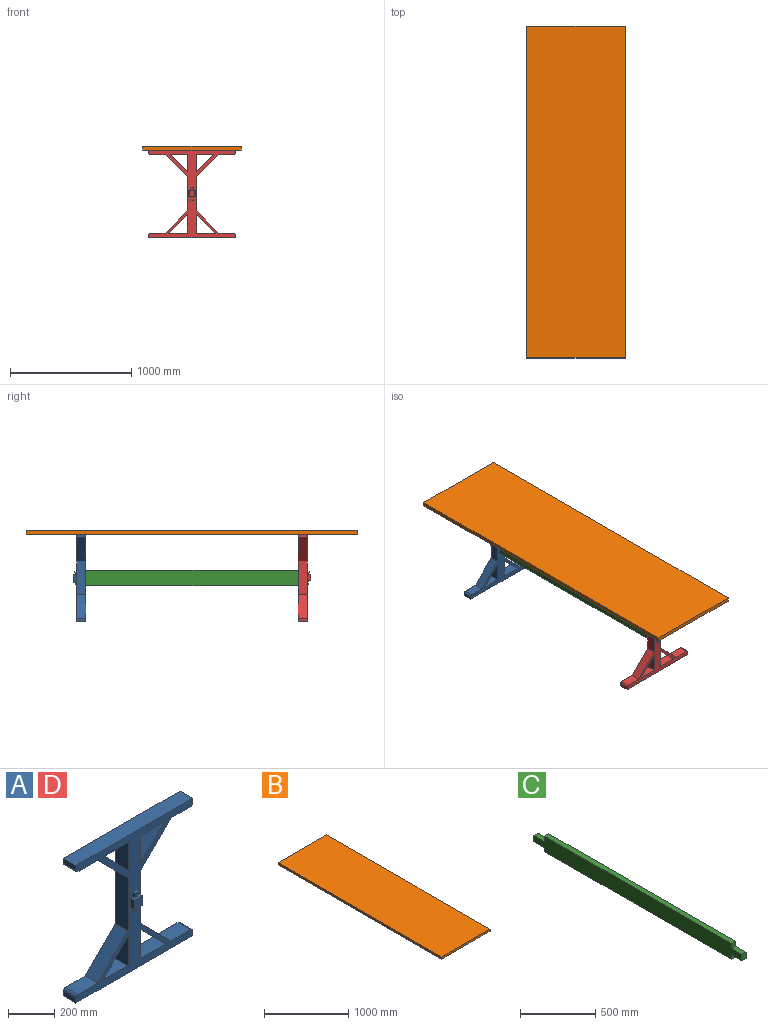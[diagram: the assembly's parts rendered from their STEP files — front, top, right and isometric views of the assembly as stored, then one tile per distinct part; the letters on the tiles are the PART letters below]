
ASSEMBLY  parts=4 mates=3
PART A: 47 faces, bbox 711.2x101.6x724.6 mm
  f0: plane 724.61x711.2mm, normal (0,-1,0), area 123856.3mm2, adj f1,f2,f3,f4,f5,f6,f7,f8
  f1: plane 50.8x25.4mm, normal (0,0,-1), area 1127mm2, adj f0,f35,f37,f38,f39,f40,f42
  f2: plane 153.23x76.2mm, normal (-1,0,0), area 11675.9mm2, adj f0,f3,f29,f34
  f3: plane 153.23x76.2mm, normal (0,0,1), area 11675.9mm2, adj f0,f2,f29,f34
  f4: plane 153.23x76.2mm, normal (0,0,1), area 11675.9mm2, adj f0,f5,f30,f34
  f5: plane 153.23x76.2mm, normal (1,0,0), area 11675.9mm2, adj f0,f4,f30,f34
  f6: plane 142.84x76.2mm, normal (1,0,0), area 10884.4mm2, adj f0,f7,f31,f34
  f7: plane 142.84x76.2mm, normal (0,0,-1), area 10884.4mm2, adj f0,f6,f31,f34
  f8: plane 142.84x142.84mm, normal (0.71,0,0.71), area 15392.8mm2, adj f0,f9,f32,f34
  f9: plane 142.84x76.2mm, normal (0,0,-1), area 10884.4mm2, adj f0,f8,f32,f34
  f10: plane 120.65x76.2mm, normal (0,0,-1), area 9193.5mm2, adj f0,f11,f33,f34
  f11: plane 184.15x184.15mm, normal (-0.71,0,-0.71), area 19844.6mm2, adj f0,f10,f12,f34
  f12: plane 280.11x76.2mm, normal (-1,0,0), area 21344.2mm2, adj f0,f11,f13,f34
  f13: plane 184.15x184.15mm, normal (-0.71,0,0.71), area 19844.6mm2, adj f0,f12,f14,f34
  f14: plane 120.65x76.2mm, normal (0,0,1), area 9193.5mm2, adj f0,f13,f15,f34
  f15: cylinder r=12.7mm len=76.2mm, axis (0,1,0), area 1520.1mm2, adj f0,f14,f16,f34
  f16: plane 76.2x25.4mm, normal (-1,0,0), area 1935.5mm2, adj f0,f15,f17,f34
  f17: plane 711.2x76.2mm, normal (0,0,-1), area 54193.4mm2, adj f0,f16,f18,f34
  f18: plane 76.2x25.4mm, normal (1,0,0), area 1935.5mm2, adj f0,f17,f19,f34
  f19: cylinder r=12.7mm len=76.2mm, axis (0,1,0), area 1520.1mm2, adj f0,f18,f20,f34
  f20: plane 120.65x76.2mm, normal (0,0,1), area 9193.5mm2, adj f0,f19,f21,f34
  f21: plane 184.15x184.15mm, normal (0.71,0,0.71), area 19844.6mm2, adj f0,f20,f22,f34
  f22: plane 280.11x76.2mm, normal (1,0,0), area 21344.2mm2, adj f0,f21,f23,f34
  f23: plane 184.15x184.15mm, normal (0.71,0,-0.71), area 19844.6mm2, adj f0,f22,f24,f34
  f24: plane 120.65x76.2mm, normal (0,0,-1), area 9193.5mm2, adj f0,f23,f25,f34
  f25: cylinder r=12.7mm len=76.2mm, axis (0,1,0), area 1520.1mm2, adj f0,f24,f26,f34
  f26: plane 76.2x25.4mm, normal (1,0,0), area 1935.5mm2, adj f0,f25,f27,f34
  f27: plane 711.2x76.2mm, normal (0,0,1), area 54193.4mm2, adj f0,f26,f28,f34
  f28: plane 76.2x25.4mm, normal (-1,0,0), area 1935.5mm2, adj f0,f27,f33,f34
  f29: plane 153.23x153.23mm, normal (0.71,0,-0.71), area 16512.1mm2, adj f0,f2,f3,f34
  f30: plane 153.23x153.23mm, normal (-0.71,0,-0.71), area 16512.1mm2, adj f0,f4,f5,f34
  f31: plane 142.84x142.84mm, normal (-0.71,0,0.71), area 15392.8mm2, adj f0,f6,f7,f34
  f32: plane 142.84x76.2mm, normal (-1,0,0), area 10884.4mm2, adj f0,f8,f9,f34
  f33: cylinder r=12.7mm len=76.2mm, axis (0,1,0), area 1520.1mm2, adj f0,f10,f28,f34
  f34: plane 724.61x711.2mm, normal (0,1,0), area 127404.7mm2, adj f2,f3,f4,f5,f6,f7,f8,f9
  f35: plane 50.8x25.4mm, normal (1,0,0), area 1290.3mm2, adj f0,f1,f36,f38
  f36: plane 50.8x25.4mm, normal (0,0,1), area 1042.4mm2, adj f0,f35,f37,f38,f43,f45,f46
  f37: plane 50.8x25.4mm, normal (-1,0,0), area 1290.3mm2, adj f0,f1,f36,f38
  f38: plane 50.8x50.8mm, normal (0,-1,0), area 2580.6mm2, adj f1,f35,f36,f37
  f39: plane 25.4x19.05mm, normal (0,-1,-0.09), area 485.7mm2, adj f1,f40,f41,f42
  f40: plane 25.4x8.57mm, normal (1,0,0), area 189.5mm2, adj f0,f1,f39,f41
  f41: plane 19.05x6.35mm, normal (0,0,-1), area 121mm2, adj f0,f39,f40,f42
  f42: plane 25.4x8.57mm, normal (-1,0,0), area 189.5mm2, adj f0,f1,f39,f41
  f43: plane 25.4x15.24mm, normal (1,0,0), area 358.8mm2, adj f0,f36,f44,f46
  f44: plane 19.05x15.24mm, normal (0,0,1), area 290.3mm2, adj f0,f43,f45,f46
  f45: plane 25.4x15.24mm, normal (-1,0,0), area 358.8mm2, adj f0,f36,f44,f46
  f46: plane 25.4x19.05mm, normal (0,-1,-0.09), area 485.7mm2, adj f36,f43,f44,f45
PART B: 6 faces, bbox 812.8x2743.2x31.8 mm
  f0: plane 2743.2x31.75mm, normal (1,0,0), area 87096.6mm2, adj f1,f3,f4,f5
  f1: plane 812.8x31.75mm, normal (0,1,0), area 25806.4mm2, adj f0,f2,f4,f5
  f2: plane 2743.2x31.75mm, normal (-1,0,0), area 87096.6mm2, adj f1,f3,f4,f5
  f3: plane 812.8x31.75mm, normal (0,-1,0), area 25806.4mm2, adj f0,f2,f4,f5
  f4: plane 2743.2x812.8mm, normal (0,0,1), area 2229673mm2, adj f0,f1,f2,f3
  f5: plane 2743.2x812.8mm, normal (0,0,-1), area 2229673mm2, adj f0,f1,f2,f3
PART C: 14 faces, bbox 38.1x1957.1x127 mm
  f0: plane 38.1x38.1mm, normal (0,-1,0), area 1451.6mm2, adj f2,f6,f7,f10
  f1: plane 38.1x38.1mm, normal (0,-1,0), area 1451.6mm2, adj f5,f6,f7,f8
  f2: plane 1752.6x38.1mm, normal (0,0,-1), area 66774.1mm2, adj f0,f3,f6,f7
  f3: plane 38.1x29.22mm, normal (0,1,-0.04), area 1114.2mm2, adj f2,f6,f7,f13
  f4: plane 46.98x38.1mm, normal (0,1,0.03), area 1790.7mm2, adj f5,f6,f7,f12
  f5: plane 1752.6x38.1mm, normal (0,0,1), area 66774.1mm2, adj f1,f4,f6,f7
  f6: plane 1957.07x127mm, normal (1,0,0), area 233015.7mm2, adj f0,f1,f2,f3,f4,f5,f8,f9
  f7: plane 1957.07x127mm, normal (-1,0,0), area 233015.7mm2, adj f0,f1,f2,f3,f4,f5,f8,f9
  f8: plane 101.6x38.1mm, normal (0,0,1), area 3871mm2, adj f1,f6,f7,f9
  f9: plane 50.8x38.1mm, normal (0,-1,0), area 1935.5mm2, adj f6,f7,f8,f10
  f10: plane 101.6x38.1mm, normal (0,0,-1), area 3871mm2, adj f0,f6,f7,f9
  f11: plane 50.8x38.1mm, normal (0,1,0), area 1935.5mm2, adj f6,f7,f12,f13
  f12: plane 101.6x38.1mm, normal (0,0,1), area 3871mm2, adj f4,f6,f7,f11
  f13: plane 101.6x38.1mm, normal (0,0,-1), area 3871mm2, adj f3,f6,f7,f11
PART D: same geometry as A
PLACE A rot(axis=(0,0,1),180deg) t=(865.79,3210.72,1014.13)mm
PLACE B t=(766.27,1036.81,1126.86)mm
PLACE C rot(axis=(-1,0,0),0deg) t=(1123.2,3172.79,723.24)mm
PLACE D rot(axis=(-1,0,0),0deg) t=(1380.61,1458.12,1014.13)mm
MATE planar A.f27 <-> B.f5  axis (0,0,1) through (1123.2,3248.82,1126.86)mm
MATE planar C.f9 <-> D.f38  axis (0,-1,0) through (1123.2,1356.52,764.91)mm
MATE planar D.f27 <-> B.f5  axis (0,0,1) through (1123.2,1420.02,1126.86)mm
